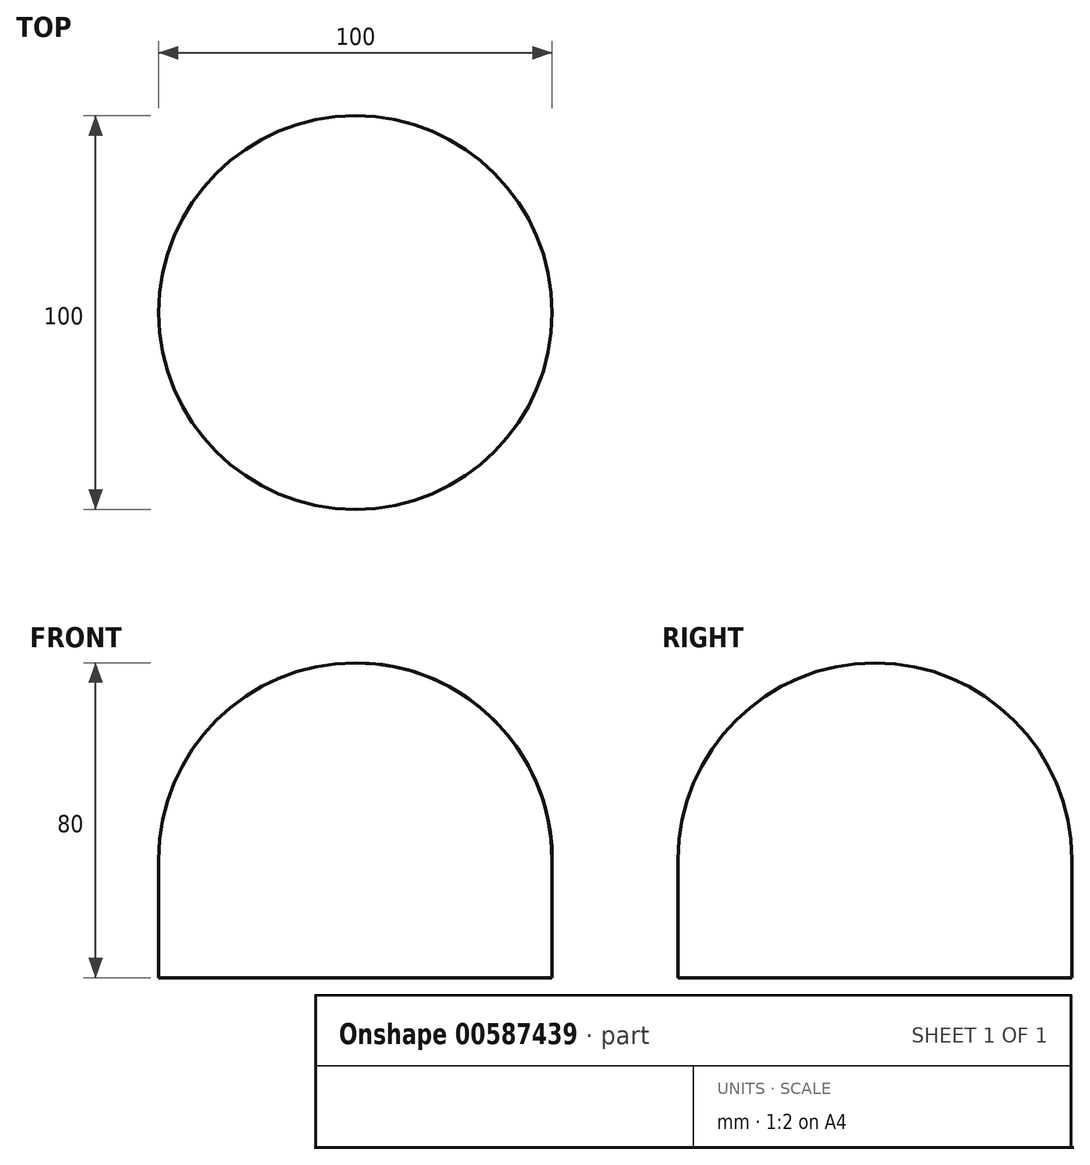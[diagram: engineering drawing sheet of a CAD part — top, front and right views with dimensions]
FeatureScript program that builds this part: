
annotation { "Feature Type Name" : "Feature", "Feature Type Description" : "" }
export const myFeature = defineFeature(function(context is Context, id is Id, definition is map)
    precondition{}
    {
        {
            var Q0;
            Q0=qCreatedBy(makeId("Front.planeOp"),FACE);
            var sketch = newSketch(context, id + "F0", { "sketchPlane" : qUnion([Q0])});
            skLineSegment(sketch, "E0", {"start": v(0, 0) * mm, "end": v(50, 0) * mm});
            skLineSegment(sketch, "E1", {"start": v(0, 0) * mm, "end": v(0, 50) * mm});
            skArc(sketch, "E2", {"start": v(50, 0) * mm, "mid": v(35.36, 35.36) * mm, "end": v(0, 50) * mm});
            skSolve(sketch);
        }
        {
            var Q0;
            Q0=qCreatedBy(makeId("Front.planeOp"),FACE);
            var sketch = newSketch(context, id + "F1", { "sketchPlane" : qUnion([Q0])});
            skLineSegment(sketch, "E3", {"start": v(0, 0) * mm, "end": v(0, 96.2) * mm});
            skSolve(sketch);
        }
        {
            var Q0;
            Q0 = qSketchRegion(id + "F0", true);
            var Q1;
            Q1=sQuery(id+"F1.wireOp",EDGE,"E3");
            revolve(context, id + "F2", {"entities" : qUnion([Q0]), "axis" : qUnion([Q1]), "revolveType" : RevolveType.FULL});
        }
        {
            var Q0;
            Q0=makeQuery(id+"F2.opRevolve","SWEPT_FACE",FACE,{"disambiguationData":[OSD([sQuery(id+"F0.wireOp",EDGE,"E0")])]});
            var sketch = newSketch(context, id + "F3", { "sketchPlane" : qUnion([Q0])});
            skCircle(sketch, "E4", {"center": v(0, 0) * mm, "radius": 50 * mm});
            skSolve(sketch);
        }
        {
            var Q0;
            Q0 = qSketchRegion(id + "F3", true);
            extrude(context, id + "F4", {"entities" : qUnion([Q0]), "operationType" : NewBodyOperationType.ADD, "depth" : 30 * mm, "offsetDistance" : 25 * mm});
        }
    });
